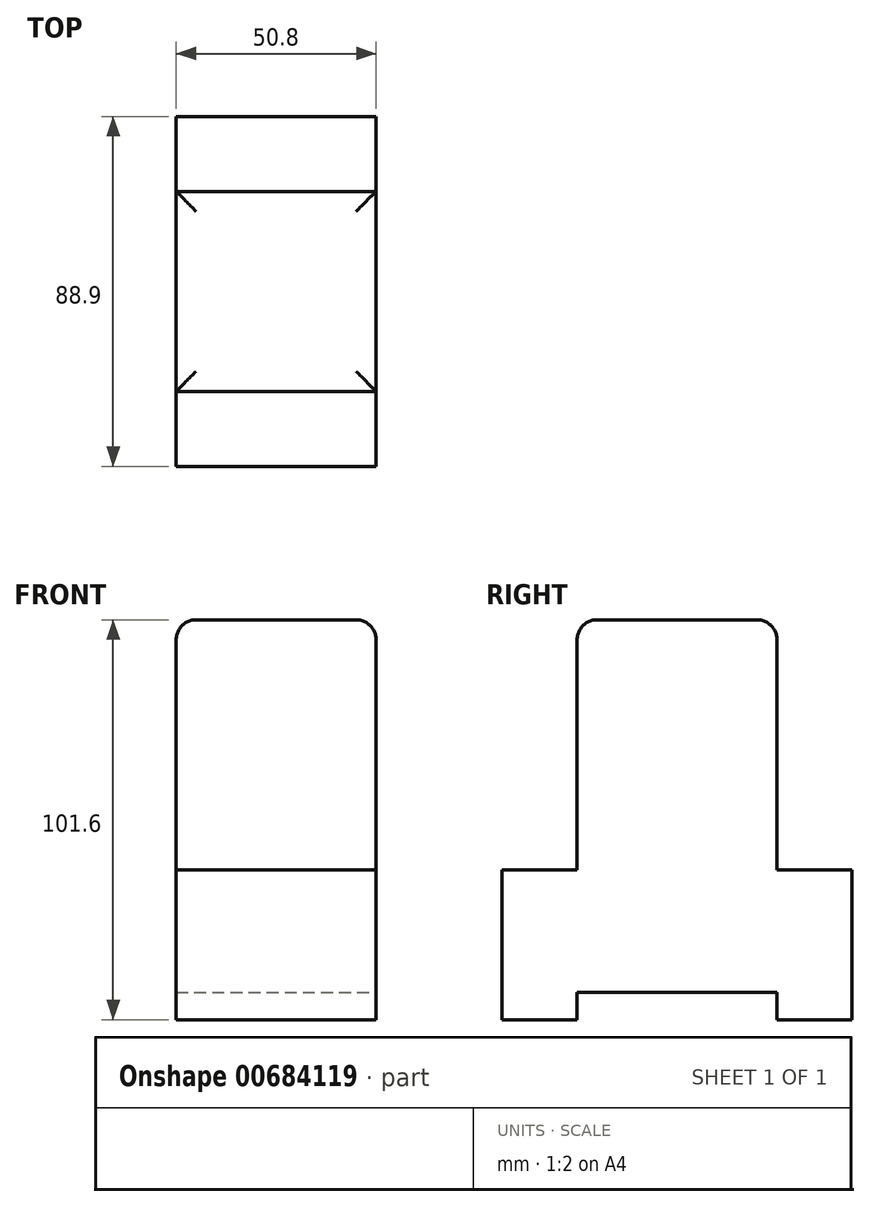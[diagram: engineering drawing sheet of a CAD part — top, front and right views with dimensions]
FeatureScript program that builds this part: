
annotation { "Feature Type Name" : "Feature", "Feature Type Description" : "" }
export const myFeature = defineFeature(function(context is Context, id is Id, definition is map)
    precondition{}
    {
        {
            var Q0;
            Q0=qCreatedBy(makeId("Top.planeOp"),FACE);
            var sketch = newSketch(context, id + "F0", { "sketchPlane" : qUnion([Q0])});
            skLineSegment(sketch, "E0.bottom", {"start": v(25.4, 44.45) * mm, "end": v(-25.4, 44.45) * mm});
            skLineSegment(sketch, "E0.top", {"start": v(25.4, -44.45) * mm, "end": v(-25.4, -44.45) * mm});
            skLineSegment(sketch, "E0.left", {"start": v(25.4, 44.45) * mm, "end": v(25.4, -44.45) * mm});
            skLineSegment(sketch, "E0.right", {"start": v(-25.4, 44.45) * mm, "end": v(-25.4, -44.45) * mm});
            skPoint(sketch, "E0.middle", {"position": v(0, 0) * mm});
            skSolve(sketch);
        }
        {
            var Q0;
            Q0 = qSketchRegion(id + "F0", true);
            extrude(context, id + "F1", {"entities" : qUnion([Q0]), "depth" : 101.6 * mm, "offsetDistance" : 25.4 * mm});
        }
        {
            var Q0;
            Q0=makeQuery(id+"F1.opExtrude","CAP_FACE",FACE,{"disambiguationData":[OSD([sQuery(id+"F0.wireOp",EDGE,"E0.bottom"),sQuery(id+"F0.wireOp",EDGE,"E0.top"),sQuery(id+"F0.wireOp",EDGE,"E0.left"),sQuery(id+"F0.wireOp",EDGE,"E0.right")])],"isStart":false});
            var sketch = newSketch(context, id + "F2", { "sketchPlane" : qUnion([Q0])});
            skLineSegment(sketch, "E1", {"start": v(-25.4, 0) * mm, "end": v(25.4, 0) * mm, "construction": true});
            skLineSegment(sketch, "E2.bottom", {"start": v(-25.4, 25.4) * mm, "end": v(25.4, 25.4) * mm});
            skLineSegment(sketch, "E2.top", {"start": v(-25.4, -25.4) * mm, "end": v(25.4, -25.4) * mm});
            skLineSegment(sketch, "E2.left", {"start": v(-25.4, 25.4) * mm, "end": v(-25.4, -25.4) * mm});
            skLineSegment(sketch, "E2.right", {"start": v(25.4, 25.4) * mm, "end": v(25.4, -25.4) * mm});
            skPoint(sketch, "E2.middle", {"position": v(0, 0) * mm});
            skSolve(sketch);
        }
        {
            var Q0;
            {var subQ0=sQuery(id+"F2.wireOp",EDGE,"E2.top");Q0=makeQuery(id+"F2.imprint","IMPRINT",FACE,{"disambiguationData":[TD([[makeQuery(id+"F2.imprint","IMPRINT",EDGE,{"derivedFrom":subQ0}),-1.0]])]});}
            var Q1;
            {var subQ0=sQuery(id+"F2.wireOp",EDGE,"E2.bottom");Q1=makeQuery(id+"F2.imprint","IMPRINT",FACE,{"disambiguationData":[TD([[makeQuery(id+"F2.imprint","IMPRINT",EDGE,{"derivedFrom":subQ0}),1.0]])]});}
            extrude(context, id + "F3", {"entities" : qUnion([Q0, Q1]), "operationType" : NewBodyOperationType.REMOVE, "oppositeDirection" : true, "depth" : 63.5 * mm, "offsetDistance" : 25.4 * mm});
        }
        {
            var Q0;
            Q0=makeQuery(id+"F1.opExtrude","SWEPT_FACE",FACE,{"disambiguationData":[OSD([sQuery(id+"F0.wireOp",EDGE,"E0.left")])]});
            var sketch = newSketch(context, id + "F4", { "sketchPlane" : qUnion([Q0])});
            skLineSegment(sketch, "E3.bottom", {"start": v(-25.4, 0) * mm, "end": v(25.4, 0) * mm});
            skLineSegment(sketch, "E3.top", {"start": v(-25.4, 6.9) * mm, "end": v(25.4, 6.9) * mm});
            skLineSegment(sketch, "E3.left", {"start": v(-25.4, 0) * mm, "end": v(-25.4, 6.9) * mm});
            skLineSegment(sketch, "E3.right", {"start": v(25.4, 0) * mm, "end": v(25.4, 6.9) * mm});
            skSolve(sketch);
        }
        {
            var Q0;
            Q0 = qSketchRegion(id + "F4", true);
            extrude(context, id + "F5", {"entities" : qUnion([Q0]), "operationType" : NewBodyOperationType.REMOVE, "oppositeDirection" : true, "depth" : 50.8 * mm, "offsetDistance" : 25.4 * mm});
        }
        {
            var Q0;
            Q0=makeQuery(id+"F1.opExtrude","CAP_FACE",FACE,{"disambiguationData":[OSD([sQuery(id+"F0.wireOp",EDGE,"E0.bottom"),sQuery(id+"F0.wireOp",EDGE,"E0.top"),sQuery(id+"F0.wireOp",EDGE,"E0.left"),sQuery(id+"F0.wireOp",EDGE,"E0.right")])],"isStart":false});
            var Q1;
            Q1=makeQuery(id+"F3.boolean.opBoolean","COPY",EDGE,{"derivedFrom":makeQuery(id+"F3.opExtrude","SWEPT_EDGE",EDGE,{"disambiguationData":[OSD([sQuery(id+"F0.wireOp",EDGE,"E0.left"),sQuery(id+"F2.wireOp",EDGE,"E2.top"),sQuery(id+"F2.wireOp",EDGE,"E2.right")])]})});
            var Q2;
            Q2=makeQuery(id+"F3.boolean.opBoolean","COPY",EDGE,{"derivedFrom":makeQuery(id+"F3.opExtrude","SWEPT_EDGE",EDGE,{"disambiguationData":[OSD([sQuery(id+"F0.wireOp",EDGE,"E0.left"),sQuery(id+"F2.wireOp",EDGE,"E2.bottom"),sQuery(id+"F2.wireOp",EDGE,"E2.right")])]})});
            var Q3;
            Q3=makeQuery(id+"F3.boolean.opBoolean","COPY",EDGE,{"derivedFrom":makeQuery(id+"F3.opExtrude","SWEPT_EDGE",EDGE,{"disambiguationData":[OSD([sQuery(id+"F0.wireOp",EDGE,"E0.right"),sQuery(id+"F2.wireOp",EDGE,"E2.bottom"),sQuery(id+"F2.wireOp",EDGE,"E2.left")])]})});
            var Q4;
            Q4=makeQuery(id+"F3.boolean.opBoolean","COPY",EDGE,{"derivedFrom":makeQuery(id+"F3.opExtrude","SWEPT_EDGE",EDGE,{"disambiguationData":[OSD([sQuery(id+"F0.wireOp",EDGE,"E0.right"),sQuery(id+"F2.wireOp",EDGE,"E2.top"),sQuery(id+"F2.wireOp",EDGE,"E2.left")])]})});
            var Q5;
            Q5=makeQuery(id+"F3.boolean.opBoolean","COPY",EDGE,{"derivedFrom":makeQuery(id+"F3.opExtrude","CAP_EDGE",EDGE,{"disambiguationData":[OSD([sQuery(id+"F0.wireOp",EDGE,"E0.top")])],"isStart":false})});
            var Q6;
            Q6=makeQuery(id+"F3.boolean.opBoolean","COPY",EDGE,{"derivedFrom":makeQuery(id+"F3.opExtrude","CAP_EDGE",EDGE,{"disambiguationData":[OSD([sQuery(id+"F0.wireOp",EDGE,"E0.bottom")])],"isStart":false})});
            fillet(context, id + "F6", {"entities" : qUnion([Q0, Q1, Q2, Q3, Q4, Q5, Q6]), "radius" : 5.08 * mm, "tangentPropagation" : true, "allowEdgeOverflow" : false});
        }
    });
